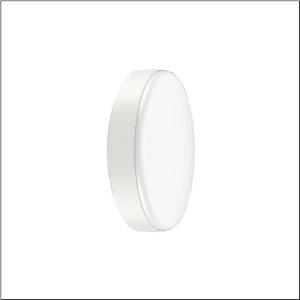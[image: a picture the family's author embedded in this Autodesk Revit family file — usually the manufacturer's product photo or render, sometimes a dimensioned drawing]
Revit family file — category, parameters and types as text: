
# Revit family: rondel_31_51wc10mb44a
name_source: partatom
category: Lighting Fixtures
units: mm (PartAtom-declared; Revit-internal decimal feet)

## family parameters
Cut with Voids When Loaded = No
Host = Face
Light Source = No
Part Type = Normal
Room Calculation Point = No
Round Connector Dimension = Use Diameter
Shared = No

## types (1)
- --- (1 x LED, 4400 lm, 34 W, 4000K)
    Apparent Load = 34 VA
    CIE Flux Codes = 44 75 94 94 100
    Color Rendering = 80
    Color Temperature = 4000K
    Default Elevation = 1800 mm
    Description = Rondel 31, wall and ceiling luminaire, primary optical cover: cover, of PC, opal, light emission: direct distribution, primary light characteristic: symmetric, installation type: surface-mounted, LED, rated luminous flux: 4.400lm, luminous efficacy: 129lm/W, light colour: 840, colour temperature: 4000K, with terminal, 3-pole, max. 2.5mm², mains connection: 220..240V, AC, 50/60Hz, rated input power: 34W, luminaire housing, of PC, traffic white (RAL 9016), diameter: 480mm, protection rating (complete): IP65, insulation class (complete): insulation class II (safety insulation), certification: CE, impact resistance: IK10, permissible operating ambient temperature: -20..+40°C, permissible storage temperature: -20..+60°C, packaging unit: 1 piece
    Height = 97 mm
    Lamp = 1 x LED
    Lamp Light Flux = 4400 lm
    Lamp Power = 34 W
    Lamp count = 1
    Length = 480 mm
    Luminous efficacy = 129 lm/W
    Manufacturer = Siteco
    ModVariant = No
    Model = 51WC10MB44A
    Mounting Place = Ceiling
    Mounting Type = Surface mounted
    Number of Poles = 1
    OnlyDefault = Yes
    Power Factor = 1
    Product Name = Rondel 31
    Product group = wall and ceiling luminaire
    ProductGroupID = 301
    Protection Class = Protection class II
    Protection Degree = IP 65
    RLX_Detail_Level = 1
    RLX_Emergency_Light_Flux = 0 lm
    RLX_Emergency_Type = 0
    RLX_Emergency_Type_DB = No
    RlxData = <blob elided: 41433 chars, md5=0b9dafc9>
    Socket = socket
    Standby Power = 0 W
    System Light Flux = 4400 lm
    System Power = 34 W
    Type Comments = factory setting: luminous flux: 100 % | (ON | ON)
    Type Image = l_1007188.jpg
    URL = http://relux.com
    VarID = @adj_083015
    Voltage = 0 V
    Weight = 0.00 kg
    Width = 0 mm  [stored 0 ft]

note: [stored X ft] marks values corroborated as IEEE doubles in the binary element streams (Revit-internal decimal feet)

## geometry (parser evidence)
native form markers: Blend x4, Sweep x14
no freeform markers — native parametric forms only
